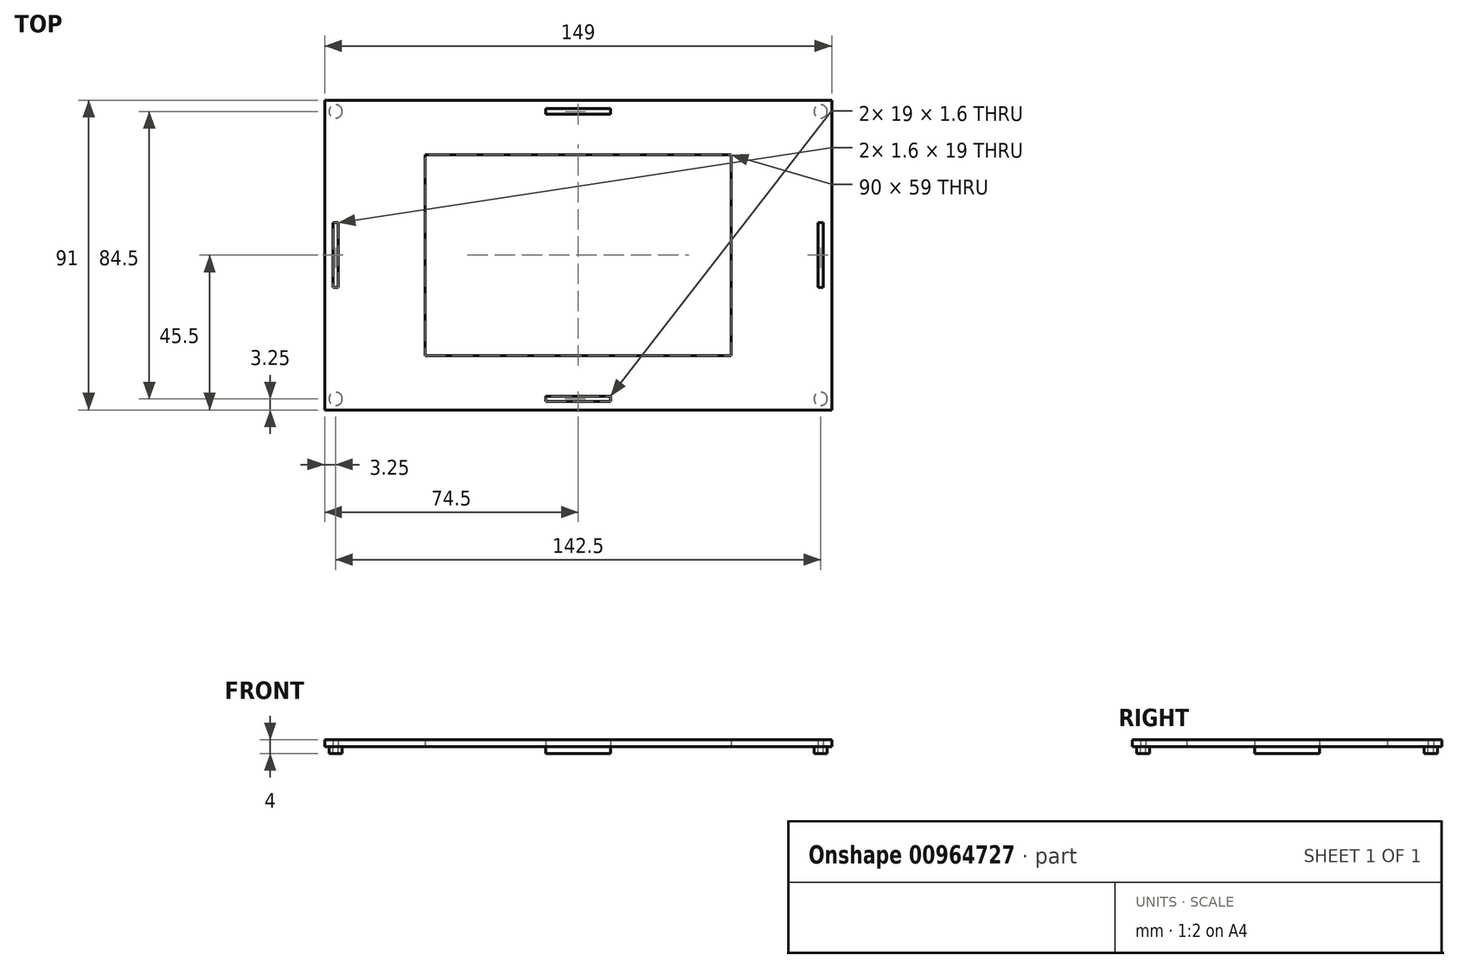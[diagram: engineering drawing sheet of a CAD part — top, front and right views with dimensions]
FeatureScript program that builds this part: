
annotation { "Feature Type Name" : "Feature", "Feature Type Description" : "" }
export const myFeature = defineFeature(function(context is Context, id is Id, definition is map)
    precondition{}
    {
        {
            var Q0;
            Q0=qCreatedBy(makeId("Top.planeOp"),FACE);
            var sketch = newSketch(context, id + "F0", { "sketchPlane" : qUnion([Q0])});
            skLineSegment(sketch, "E0.bottom", {"start": v(74.5, -45.5) * mm, "end": v(-74.5, -45.5) * mm});
            skLineSegment(sketch, "E0.top", {"start": v(74.5, 45.5) * mm, "end": v(-74.5, 45.5) * mm});
            skLineSegment(sketch, "E0.left", {"start": v(74.5, -45.5) * mm, "end": v(74.5, 45.5) * mm});
            skLineSegment(sketch, "E0.right", {"start": v(-74.5, -45.5) * mm, "end": v(-74.5, 45.5) * mm});
            skPoint(sketch, "E0.middle", {"position": v(0, 0) * mm});
            skLineSegment(sketch, "E1.bottom", {"start": v(68, -39) * mm, "end": v(-68, -39) * mm});
            skLineSegment(sketch, "E1.top", {"start": v(68, 39) * mm, "end": v(-68, 39) * mm});
            skLineSegment(sketch, "E1.left", {"start": v(68, -39) * mm, "end": v(68, 39) * mm});
            skLineSegment(sketch, "E1.right", {"start": v(-68, -39) * mm, "end": v(-68, 39) * mm});
            skLineSegment(sketch, "E2", {"start": v(74.5, 45.5) * mm, "end": v(68, 39) * mm});
            skLineSegment(sketch, "E3", {"start": v(-74.5, 45.5) * mm, "end": v(-68, 39) * mm});
            skLineSegment(sketch, "E4", {"start": v(-68, -39) * mm, "end": v(-74.5, -45.5) * mm});
            skLineSegment(sketch, "E5", {"start": v(68, -39) * mm, "end": v(74.5, -45.5) * mm});
            skLineSegment(sketch, "E6.bottom", {"start": v(45, -29.5) * mm, "end": v(-45, -29.5) * mm});
            skLineSegment(sketch, "E6.top", {"start": v(45, 29.5) * mm, "end": v(-45, 29.5) * mm});
            skLineSegment(sketch, "E6.left", {"start": v(45, -29.5) * mm, "end": v(45, 29.5) * mm});
            skLineSegment(sketch, "E6.right", {"start": v(-45, -29.5) * mm, "end": v(-45, 29.5) * mm});
            skCircle(sketch, "E7", {"center": v(-71.25, 42.25) * mm, "radius": 1.95 * mm});
            skCircle(sketch, "E8", {"center": v(71.25, 42.25) * mm, "radius": 1.95 * mm});
            skCircle(sketch, "E9", {"center": v(-71.25, -42.25) * mm, "radius": 1.95 * mm});
            skCircle(sketch, "E10", {"center": v(71.25, -42.25) * mm, "radius": 1.95 * mm});
            skLineSegment(sketch, "E11", {"start": v(0, 39) * mm, "end": v(0, 29.5) * mm});
            skLineSegment(sketch, "E12", {"start": v(-45, 0) * mm, "end": v(-68, 0) * mm});
            skLineSegment(sketch, "E13", {"start": v(45, 0) * mm, "end": v(68, 0) * mm});
            skLineSegment(sketch, "E14", {"start": v(0, -29.5) * mm, "end": v(0, -39) * mm});
            skLineSegment(sketch, "E15", {"start": v(-68, 0) * mm, "end": v(-74.5, 0) * mm});
            skLineSegment(sketch, "E16", {"start": v(0, -39) * mm, "end": v(0, -45.5) * mm});
            skLineSegment(sketch, "E17", {"start": v(74.5, 0) * mm, "end": v(68, 0) * mm});
            skLineSegment(sketch, "E18", {"start": v(0, 45.5) * mm, "end": v(0, 39) * mm});
            skPoint(sketch, "E19", {"position": v(0, 42.25) * mm});
            skPoint(sketch, "E20", {"position": v(71.25, 0) * mm});
            skPoint(sketch, "E21", {"position": v(0, -42.25) * mm});
            skPoint(sketch, "E22", {"position": v(-71.25, 0) * mm});
            skLineSegment(sketch, "E23.bottom", {"start": v(9.5, 41.45) * mm, "end": v(-9.5, 41.45) * mm});
            skLineSegment(sketch, "E23.top", {"start": v(9.5, 43.05) * mm, "end": v(-9.5, 43.05) * mm});
            skLineSegment(sketch, "E23.left", {"start": v(9.5, 41.45) * mm, "end": v(9.5, 43.05) * mm});
            skLineSegment(sketch, "E23.right", {"start": v(-9.5, 41.45) * mm, "end": v(-9.5, 43.05) * mm});
            skLineSegment(sketch, "E24.bottom", {"start": v(-70.45, 9.5) * mm, "end": v(-72.05, 9.5) * mm});
            skLineSegment(sketch, "E24.top", {"start": v(-70.45, -9.5) * mm, "end": v(-72.05, -9.5) * mm});
            skLineSegment(sketch, "E24.left", {"start": v(-70.45, 9.5) * mm, "end": v(-70.45, -9.5) * mm});
            skLineSegment(sketch, "E24.right", {"start": v(-72.05, 9.5) * mm, "end": v(-72.05, -9.5) * mm});
            skLineSegment(sketch, "E25.bottom", {"start": v(72.05, -9.5) * mm, "end": v(70.45, -9.5) * mm});
            skLineSegment(sketch, "E25.top", {"start": v(72.05, 9.5) * mm, "end": v(70.45, 9.5) * mm});
            skLineSegment(sketch, "E25.left", {"start": v(72.05, -9.5) * mm, "end": v(72.05, 9.5) * mm});
            skLineSegment(sketch, "E25.right", {"start": v(70.45, -9.5) * mm, "end": v(70.45, 9.5) * mm});
            skLineSegment(sketch, "E26.bottom", {"start": v(9.5, -43.05) * mm, "end": v(-9.5, -43.05) * mm});
            skLineSegment(sketch, "E26.top", {"start": v(9.5, -41.45) * mm, "end": v(-9.5, -41.45) * mm});
            skLineSegment(sketch, "E26.left", {"start": v(9.5, -43.05) * mm, "end": v(9.5, -41.45) * mm});
            skLineSegment(sketch, "E26.right", {"start": v(-9.5, -43.05) * mm, "end": v(-9.5, -41.45) * mm});
            skSolve(sketch);
        }
        {
            var Q0;
            Q0=makeQuery(id+"F0.imprint","IMPRINT",FACE,{"disambiguationData":[TD([[makeQuery(id+"F0.imprint","IMPRINT",EDGE,{"derivedFrom":sQuery(id+"F0.wireOp",EDGE,"E1.bottom")}),-1.0]])]});
            var Q1;
            Q1=makeQuery(id+"F0.imprint","IMPRINT",FACE,{"disambiguationData":[TD([[makeQuery(id+"F0.imprint","IMPRINT",EDGE,{"derivedFrom":sQuery(id+"F0.wireOp",EDGE,"E6.bottom")}),-1.0]])]});
            var Q2;
            {var subQ8=sQuery(id+"F0.wireOp",EDGE,"E0.bottom");Q2=makeQuery(id+"F0.imprint","IMPRINT",FACE,{"disambiguationData":[TD([[makeQuery(id+"F0.imprint","IMPRINT",EDGE,{"derivedFrom":subQ8}),-1.0]])]});}
            var Q3;
            {var subQ1=sQuery(id+"F0.wireOp",EDGE,"E0.top");Q3=makeQuery(id+"F0.imprint","IMPRINT",FACE,{"disambiguationData":[TD([[makeQuery(id+"F0.imprint","IMPRINT",EDGE,{"derivedFrom":subQ1}),1.0]])]});}
            var Q4;
            {var subQ4=sQuery(id+"F0.wireOp",EDGE,"E0.left");Q4=makeQuery(id+"F0.imprint","IMPRINT",FACE,{"disambiguationData":[TD([[makeQuery(id+"F0.imprint","IMPRINT",EDGE,{"derivedFrom":subQ4}),1.0]])]});}
            var Q5;
            {var subQ7=sQuery(id+"F0.wireOp",EDGE,"E0.right");Q5=makeQuery(id+"F0.imprint","IMPRINT",FACE,{"disambiguationData":[TD([[makeQuery(id+"F0.imprint","IMPRINT",EDGE,{"derivedFrom":subQ7}),-1.0]])]});}
            var Q6;
            {var subQ0=sQuery(id+"F0.wireOp",EDGE,"u4o9W65d-h8mD-DEjK-P3O9-7eLyaXnTy4Te");var subQ1=sQuery(id+"F0.wireOp",EDGE,"E2");var subQ2=makeQuery(id+"F0.imprint","INTERSECT",VERTEX,{"disambiguationData":[OD(0.0)],"derivedFrom":[subQ1,subQ0]});Q6=makeQuery(id+"F0.imprint","IMPRINT",FACE,{"disambiguationData":[TD([[makeQuery(id+"F0.imprint","IMPRINT",EDGE,{"disambiguationData":[TD([[subQ2,-1.0]])],"derivedFrom":subQ1}),-1.0]])]});}
            var Q7;
            {var subQ0=sQuery(id+"F0.wireOp",EDGE,"u4o9W65d-h8mD-DEjK-P3O9-7eLyaXnTy4Te");var subQ1=sQuery(id+"F0.wireOp",EDGE,"E2");var subQ2=makeQuery(id+"F0.imprint","INTERSECT",VERTEX,{"disambiguationData":[OD(0.0)],"derivedFrom":[subQ1,subQ0]});Q7=makeQuery(id+"F0.imprint","IMPRINT",FACE,{"disambiguationData":[TD([[makeQuery(id+"F0.imprint","IMPRINT",EDGE,{"disambiguationData":[TD([[subQ2,-1.0]])],"derivedFrom":subQ1}),1.0]])]});}
            var Q8;
            {var subQ0=sQuery(id+"F0.wireOp",EDGE,"lMdRnU9m-Uv7t-4uh5-qnpr-yOsPV0Vjd2ES");var subQ1=sQuery(id+"F0.wireOp",EDGE,"E3");var subQ2=makeQuery(id+"F0.imprint","INTERSECT",VERTEX,{"disambiguationData":[OD(0.0)],"derivedFrom":[subQ1,subQ0]});Q8=makeQuery(id+"F0.imprint","IMPRINT",FACE,{"disambiguationData":[TD([[makeQuery(id+"F0.imprint","IMPRINT",EDGE,{"disambiguationData":[TD([[subQ2,-1.0]])],"derivedFrom":subQ1}),-1.0]])]});}
            var Q9;
            {var subQ0=sQuery(id+"F0.wireOp",EDGE,"lMdRnU9m-Uv7t-4uh5-qnpr-yOsPV0Vjd2ES");var subQ1=sQuery(id+"F0.wireOp",EDGE,"E3");var subQ2=makeQuery(id+"F0.imprint","INTERSECT",VERTEX,{"disambiguationData":[OD(0.0)],"derivedFrom":[subQ1,subQ0]});Q9=makeQuery(id+"F0.imprint","IMPRINT",FACE,{"disambiguationData":[TD([[makeQuery(id+"F0.imprint","IMPRINT",EDGE,{"disambiguationData":[TD([[subQ2,-1.0]])],"derivedFrom":subQ1}),1.0]])]});}
            var Q10;
            {var subQ0=sQuery(id+"F0.wireOp",EDGE,"v2OHcP9R-Ypyw-fKLo-QjBW-63Kn7PKXuLIF");var subQ1=sQuery(id+"F0.wireOp",EDGE,"E4");var subQ2=makeQuery(id+"F0.imprint","INTERSECT",VERTEX,{"disambiguationData":[OD(0.0)],"derivedFrom":[subQ1,subQ0]});Q10=makeQuery(id+"F0.imprint","IMPRINT",FACE,{"disambiguationData":[TD([[makeQuery(id+"F0.imprint","IMPRINT",EDGE,{"disambiguationData":[TD([[subQ2,-1.0]])],"derivedFrom":subQ1}),-1.0]])]});}
            var Q11;
            {var subQ0=sQuery(id+"F0.wireOp",EDGE,"v2OHcP9R-Ypyw-fKLo-QjBW-63Kn7PKXuLIF");var subQ1=sQuery(id+"F0.wireOp",EDGE,"E4");var subQ2=makeQuery(id+"F0.imprint","INTERSECT",VERTEX,{"disambiguationData":[OD(0.0)],"derivedFrom":[subQ1,subQ0]});Q11=makeQuery(id+"F0.imprint","IMPRINT",FACE,{"disambiguationData":[TD([[makeQuery(id+"F0.imprint","IMPRINT",EDGE,{"disambiguationData":[TD([[subQ2,-1.0]])],"derivedFrom":subQ1}),1.0]])]});}
            var Q12;
            {var subQ0=sQuery(id+"F0.wireOp",EDGE,"DEakPpWx-NRV0-5eK2-LGjB-KXZnGJ3cSSGY");var subQ1=sQuery(id+"F0.wireOp",EDGE,"E5");var subQ2=makeQuery(id+"F0.imprint","INTERSECT",VERTEX,{"disambiguationData":[OD(0.0)],"derivedFrom":[subQ1,subQ0]});Q12=makeQuery(id+"F0.imprint","IMPRINT",FACE,{"disambiguationData":[TD([[makeQuery(id+"F0.imprint","IMPRINT",EDGE,{"disambiguationData":[TD([[subQ2,-1.0]])],"derivedFrom":subQ1}),-1.0]])]});}
            var Q13;
            {var subQ0=sQuery(id+"F0.wireOp",EDGE,"DEakPpWx-NRV0-5eK2-LGjB-KXZnGJ3cSSGY");var subQ1=sQuery(id+"F0.wireOp",EDGE,"E5");var subQ2=makeQuery(id+"F0.imprint","INTERSECT",VERTEX,{"disambiguationData":[OD(0.0)],"derivedFrom":[subQ1,subQ0]});Q13=makeQuery(id+"F0.imprint","IMPRINT",FACE,{"disambiguationData":[TD([[makeQuery(id+"F0.imprint","IMPRINT",EDGE,{"disambiguationData":[TD([[subQ2,-1.0]])],"derivedFrom":subQ1}),1.0]])]});}
            var Q14;
            {var subQ7=sQuery(id+"F0.wireOp",EDGE,"E11");Q14=makeQuery(id+"F0.imprint","IMPRINT",FACE,{"disambiguationData":[TD([[makeQuery(id+"F0.imprint","IMPRINT",EDGE,{"derivedFrom":subQ7}),-1.0]])]});}
            var Q15;
            {var subQ4=sQuery(id+"F0.wireOp",EDGE,"E11");Q15=makeQuery(id+"F0.imprint","IMPRINT",FACE,{"disambiguationData":[TD([[makeQuery(id+"F0.imprint","IMPRINT",EDGE,{"derivedFrom":subQ4}),1.0]])]});}
            extrude(context, id + "F1", {"entities" : qUnion([Q0, Q1, Q2, Q3, Q4, Q5, Q6, Q7, Q8, Q9, Q10, Q11, Q12, Q13, Q14, Q15]), "depth" : 2 * mm, "offsetDistance" : 25 * mm});
        }
        {
            var Q0;
            Q0=makeQuery(id+"F0.imprint","IMPRINT",FACE,{"disambiguationData":[TD([[makeQuery(id+"F0.imprint","IMPRINT",EDGE,{"derivedFrom":sQuery(id+"F0.wireOp",EDGE,"E6.bottom")}),-1.0]])]});
            extrude(context, id + "F2", {"entities" : qUnion([Q0]), "operationType" : NewBodyOperationType.REMOVE, "depth" : 5 * mm, "offsetDistance" : 25 * mm});
        }
        {
            var Q0;
            {var subQ0=sQuery(id+"F0.wireOp",EDGE,"E8");var subQ1=sQuery(id+"F0.wireOp",EDGE,"E2");var subQ2=makeQuery(id+"F0.imprint","INTERSECT",VERTEX,{"disambiguationData":[OD(0.0)],"derivedFrom":[subQ1,subQ0]});Q0=makeQuery(id+"F0.imprint","IMPRINT",FACE,{"disambiguationData":[TD([[makeQuery(id+"F0.imprint","IMPRINT",EDGE,{"disambiguationData":[TD([[subQ2,-1.0]])],"derivedFrom":subQ1}),1.0]])]});}
            var Q1;
            {var subQ0=sQuery(id+"F0.wireOp",EDGE,"E8");var subQ1=sQuery(id+"F0.wireOp",EDGE,"E2");var subQ2=makeQuery(id+"F0.imprint","INTERSECT",VERTEX,{"disambiguationData":[OD(0.0)],"derivedFrom":[subQ1,subQ0]});Q1=makeQuery(id+"F0.imprint","IMPRINT",FACE,{"disambiguationData":[TD([[makeQuery(id+"F0.imprint","IMPRINT",EDGE,{"disambiguationData":[TD([[subQ2,-1.0]])],"derivedFrom":subQ1}),-1.0]])]});}
            var Q2;
            {var subQ0=sQuery(id+"F0.wireOp",EDGE,"E7");var subQ1=sQuery(id+"F0.wireOp",EDGE,"E3");var subQ2=makeQuery(id+"F0.imprint","INTERSECT",VERTEX,{"disambiguationData":[OD(0.0)],"derivedFrom":[subQ1,subQ0]});Q2=makeQuery(id+"F0.imprint","IMPRINT",FACE,{"disambiguationData":[TD([[makeQuery(id+"F0.imprint","IMPRINT",EDGE,{"disambiguationData":[TD([[subQ2,-1.0]])],"derivedFrom":subQ1}),-1.0]])]});}
            var Q3;
            {var subQ0=sQuery(id+"F0.wireOp",EDGE,"E7");var subQ1=sQuery(id+"F0.wireOp",EDGE,"E3");var subQ2=makeQuery(id+"F0.imprint","INTERSECT",VERTEX,{"disambiguationData":[OD(0.0)],"derivedFrom":[subQ1,subQ0]});Q3=makeQuery(id+"F0.imprint","IMPRINT",FACE,{"disambiguationData":[TD([[makeQuery(id+"F0.imprint","IMPRINT",EDGE,{"disambiguationData":[TD([[subQ2,-1.0]])],"derivedFrom":subQ1}),1.0]])]});}
            var Q4;
            {var subQ0=sQuery(id+"F0.wireOp",EDGE,"E9");var subQ1=sQuery(id+"F0.wireOp",EDGE,"E4");var subQ2=makeQuery(id+"F0.imprint","INTERSECT",VERTEX,{"disambiguationData":[OD(0.0)],"derivedFrom":[subQ1,subQ0]});Q4=makeQuery(id+"F0.imprint","IMPRINT",FACE,{"disambiguationData":[TD([[makeQuery(id+"F0.imprint","IMPRINT",EDGE,{"disambiguationData":[TD([[subQ2,-1.0]])],"derivedFrom":subQ1}),1.0]])]});}
            var Q5;
            {var subQ0=sQuery(id+"F0.wireOp",EDGE,"E9");var subQ1=sQuery(id+"F0.wireOp",EDGE,"E4");var subQ2=makeQuery(id+"F0.imprint","INTERSECT",VERTEX,{"disambiguationData":[OD(0.0)],"derivedFrom":[subQ1,subQ0]});Q5=makeQuery(id+"F0.imprint","IMPRINT",FACE,{"disambiguationData":[TD([[makeQuery(id+"F0.imprint","IMPRINT",EDGE,{"disambiguationData":[TD([[subQ2,-1.0]])],"derivedFrom":subQ1}),-1.0]])]});}
            var Q6;
            {var subQ0=sQuery(id+"F0.wireOp",EDGE,"E10");var subQ1=sQuery(id+"F0.wireOp",EDGE,"E5");var subQ2=makeQuery(id+"F0.imprint","INTERSECT",VERTEX,{"disambiguationData":[OD(0.0)],"derivedFrom":[subQ1,subQ0]});Q6=makeQuery(id+"F0.imprint","IMPRINT",FACE,{"disambiguationData":[TD([[makeQuery(id+"F0.imprint","IMPRINT",EDGE,{"disambiguationData":[TD([[subQ2,-1.0]])],"derivedFrom":subQ1}),-1.0]])]});}
            var Q7;
            {var subQ0=sQuery(id+"F0.wireOp",EDGE,"E10");var subQ1=sQuery(id+"F0.wireOp",EDGE,"E5");var subQ2=makeQuery(id+"F0.imprint","INTERSECT",VERTEX,{"disambiguationData":[OD(0.0)],"derivedFrom":[subQ1,subQ0]});Q7=makeQuery(id+"F0.imprint","IMPRINT",FACE,{"disambiguationData":[TD([[makeQuery(id+"F0.imprint","IMPRINT",EDGE,{"disambiguationData":[TD([[subQ2,-1.0]])],"derivedFrom":subQ1}),1.0]])]});}
            var Q8;
            {var subQ5=sQuery(id+"F0.wireOp",EDGE,"E24.top");Q8=makeQuery(id+"F0.imprint","IMPRINT",FACE,{"disambiguationData":[TD([[makeQuery(id+"F0.imprint","IMPRINT",EDGE,{"derivedFrom":subQ5}),-1.0]])]});}
            var Q9;
            {var subQ5=sQuery(id+"F0.wireOp",EDGE,"E24.bottom");Q9=makeQuery(id+"F0.imprint","IMPRINT",FACE,{"disambiguationData":[TD([[makeQuery(id+"F0.imprint","IMPRINT",EDGE,{"derivedFrom":subQ5}),1.0]])]});}
            var Q10;
            {var subQ5=sQuery(id+"F0.wireOp",EDGE,"E23.right");Q10=makeQuery(id+"F0.imprint","IMPRINT",FACE,{"disambiguationData":[TD([[makeQuery(id+"F0.imprint","IMPRINT",EDGE,{"derivedFrom":subQ5}),-1.0]])]});}
            var Q11;
            {var subQ5=sQuery(id+"F0.wireOp",EDGE,"E23.left");Q11=makeQuery(id+"F0.imprint","IMPRINT",FACE,{"disambiguationData":[TD([[makeQuery(id+"F0.imprint","IMPRINT",EDGE,{"derivedFrom":subQ5}),1.0]])]});}
            var Q12;
            {var subQ5=sQuery(id+"F0.wireOp",EDGE,"E25.top");Q12=makeQuery(id+"F0.imprint","IMPRINT",FACE,{"disambiguationData":[TD([[makeQuery(id+"F0.imprint","IMPRINT",EDGE,{"derivedFrom":subQ5}),1.0]])]});}
            var Q13;
            {var subQ5=sQuery(id+"F0.wireOp",EDGE,"E25.bottom");Q13=makeQuery(id+"F0.imprint","IMPRINT",FACE,{"disambiguationData":[TD([[makeQuery(id+"F0.imprint","IMPRINT",EDGE,{"derivedFrom":subQ5}),-1.0]])]});}
            var Q14;
            {var subQ5=sQuery(id+"F0.wireOp",EDGE,"E26.left");Q14=makeQuery(id+"F0.imprint","IMPRINT",FACE,{"disambiguationData":[TD([[makeQuery(id+"F0.imprint","IMPRINT",EDGE,{"derivedFrom":subQ5}),1.0]])]});}
            var Q15;
            {var subQ5=sQuery(id+"F0.wireOp",EDGE,"E26.right");Q15=makeQuery(id+"F0.imprint","IMPRINT",FACE,{"disambiguationData":[TD([[makeQuery(id+"F0.imprint","IMPRINT",EDGE,{"derivedFrom":subQ5}),-1.0]])]});}
            extrude(context, id + "F3", {"entities" : qUnion([Q0, Q1, Q2, Q3, Q4, Q5, Q6, Q7, Q8, Q9, Q10, Q11, Q12, Q13, Q14, Q15]), "operationType" : NewBodyOperationType.ADD, "oppositeDirection" : true, "depth" : 2 * mm, "offsetDistance" : 25 * mm});
        }
        {
            var Q0;
            {var subQ5=sQuery(id+"F0.wireOp",EDGE,"E23.right");Q0=makeQuery(id+"F0.imprint","IMPRINT",FACE,{"disambiguationData":[TD([[makeQuery(id+"F0.imprint","IMPRINT",EDGE,{"derivedFrom":subQ5}),-1.0]])]});}
            var Q1;
            {var subQ5=sQuery(id+"F0.wireOp",EDGE,"E23.left");Q1=makeQuery(id+"F0.imprint","IMPRINT",FACE,{"disambiguationData":[TD([[makeQuery(id+"F0.imprint","IMPRINT",EDGE,{"derivedFrom":subQ5}),1.0]])]});}
            var Q2;
            {var subQ5=sQuery(id+"F0.wireOp",EDGE,"E24.bottom");Q2=makeQuery(id+"F0.imprint","IMPRINT",FACE,{"disambiguationData":[TD([[makeQuery(id+"F0.imprint","IMPRINT",EDGE,{"derivedFrom":subQ5}),1.0]])]});}
            var Q3;
            {var subQ5=sQuery(id+"F0.wireOp",EDGE,"E24.top");Q3=makeQuery(id+"F0.imprint","IMPRINT",FACE,{"disambiguationData":[TD([[makeQuery(id+"F0.imprint","IMPRINT",EDGE,{"derivedFrom":subQ5}),-1.0]])]});}
            var Q4;
            {var subQ5=sQuery(id+"F0.wireOp",EDGE,"E25.top");Q4=makeQuery(id+"F0.imprint","IMPRINT",FACE,{"disambiguationData":[TD([[makeQuery(id+"F0.imprint","IMPRINT",EDGE,{"derivedFrom":subQ5}),1.0]])]});}
            var Q5;
            {var subQ5=sQuery(id+"F0.wireOp",EDGE,"E25.bottom");Q5=makeQuery(id+"F0.imprint","IMPRINT",FACE,{"disambiguationData":[TD([[makeQuery(id+"F0.imprint","IMPRINT",EDGE,{"derivedFrom":subQ5}),-1.0]])]});}
            var Q6;
            {var subQ5=sQuery(id+"F0.wireOp",EDGE,"E26.right");Q6=makeQuery(id+"F0.imprint","IMPRINT",FACE,{"disambiguationData":[TD([[makeQuery(id+"F0.imprint","IMPRINT",EDGE,{"derivedFrom":subQ5}),-1.0]])]});}
            var Q7;
            {var subQ5=sQuery(id+"F0.wireOp",EDGE,"E26.left");Q7=makeQuery(id+"F0.imprint","IMPRINT",FACE,{"disambiguationData":[TD([[makeQuery(id+"F0.imprint","IMPRINT",EDGE,{"derivedFrom":subQ5}),1.0]])]});}
            extrude(context, id + "F4", {"entities" : qUnion([Q0, Q1, Q2, Q3, Q4, Q5, Q6, Q7]), "depth" : 2 * mm, "offsetDistance" : 25 * mm});
        }
    });
